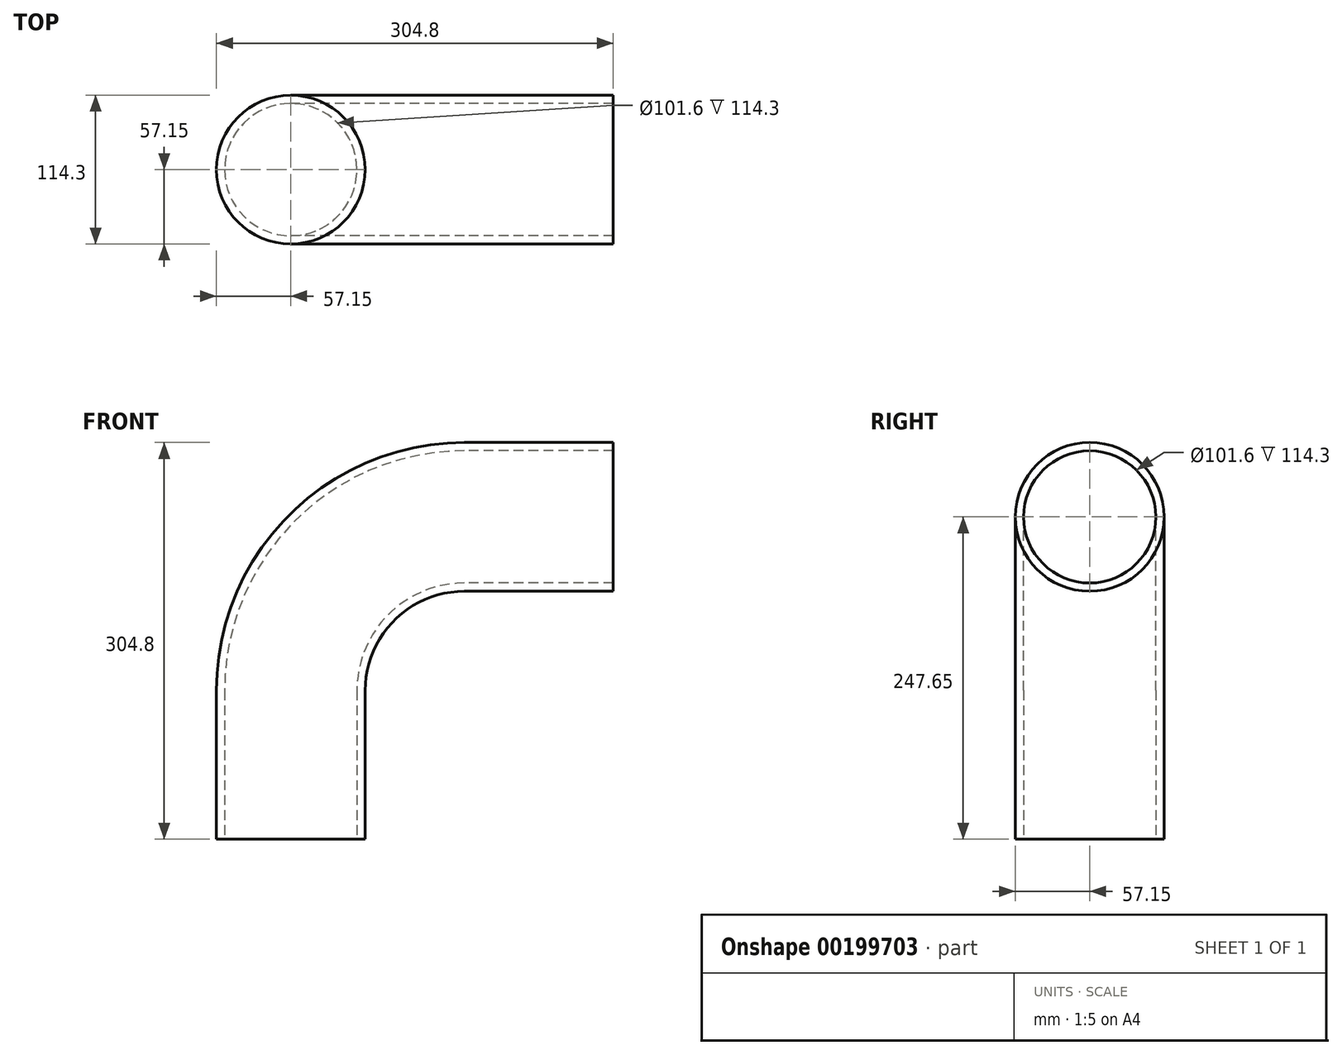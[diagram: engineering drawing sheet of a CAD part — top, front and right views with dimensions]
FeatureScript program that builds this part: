
annotation { "Feature Type Name" : "Feature", "Feature Type Description" : "" }
export const myFeature = defineFeature(function(context is Context, id is Id, definition is map)
    precondition{}
    {
        {
            var Q0;
            Q0=qCreatedBy(makeId("Front.planeOp"),FACE);
            var sketch = newSketch(context, id + "F0", { "sketchPlane" : qUnion([Q0])});
            skLineSegment(sketch, "E0.bottom", {"start": v(0, 0) * mm, "end": v(114.3, 0) * mm});
            skLineSegment(sketch, "E0.top", {"start": v(190.5, 304.8) * mm, "end": v(304.8, 304.8) * mm});
            skLineSegment(sketch, "E0.left", {"start": v(0, 0) * mm, "end": v(0, 114.3) * mm});
            skLineSegment(sketch, "E0.right", {"start": v(304.8, 190.5) * mm, "end": v(304.8, 304.8) * mm});
            skLineSegment(sketch, "E1.right", {"start": v(114.3, 0) * mm, "end": v(114.3, 114.3) * mm});
            skLineSegment(sketch, "E2.top", {"start": v(304.8, 190.5) * mm, "end": v(190.5, 190.5) * mm});
            skArc(sketch, "E3", {"start": v(190.5, 190.5) * mm, "mid": v(136.62, 168.18) * mm, "end": v(114.3, 114.3) * mm});
            skArc(sketch, "E4", {"start": v(190.5, 304.8) * mm, "mid": v(55.8, 249) * mm, "end": v(0, 114.3) * mm});
            skSolve(sketch);
        }
        {
            var Q0;
            Q0=makeQuery(id+"F0.imprint","IMPRINT",FACE,{"disambiguationData":[TD([[makeQuery(id+"F0.imprint","IMPRINT",EDGE,{"derivedFrom":sQuery(id+"F0.wireOp",EDGE,"E0.bottom")}),1.0]])]});
            extrude(context, id + "F1", {"entities" : qUnion([Q0]), "endBound" : BoundingType.SYMMETRIC, "depth" : 114.3 * mm});
        }
        {
            var Q0;
            Q0=makeQuery(id+"F1.opExtrude","CAP_EDGE",EDGE,{"disambiguationData":[OSD([sQuery(id+"F0.wireOp",EDGE,"E1.right")])],"isStart":false});
            var Q1;
            Q1=makeQuery(id+"F1.opExtrude","CAP_EDGE",EDGE,{"disambiguationData":[OSD([sQuery(id+"F0.wireOp",EDGE,"E1.right")])],"isStart":true});
            var Q2;
            Q2=makeQuery(id+"F1.opExtrude","CAP_EDGE",EDGE,{"disambiguationData":[OSD([sQuery(id+"F0.wireOp",EDGE,"E0.top")])],"isStart":false});
            var Q3;
            Q3=makeQuery(id+"F1.opExtrude","CAP_EDGE",EDGE,{"disambiguationData":[OSD([sQuery(id+"F0.wireOp",EDGE,"E0.top")])],"isStart":true});
            fillet(context, id + "F2", {"entities" : qUnion([Q0, Q1, Q2, Q3]), "radius" : 57.15 * mm, "tangentPropagation" : true, "allowEdgeOverflow" : false});
        }
        {
            var Q0;
            Q0=makeQuery(id+"F1.opExtrude","SWEPT_FACE",FACE,{"disambiguationData":[OSD([sQuery(id+"F0.wireOp",EDGE,"E0.right")])]});
            var Q1;
            Q1=makeQuery(id+"F1.opExtrude","SWEPT_FACE",FACE,{"disambiguationData":[OSD([sQuery(id+"F0.wireOp",EDGE,"E0.bottom")])]});
            shell(context, id + "F3", {"entities" : qUnion([Q0, Q1]), "thickness" : 6.35 * mm});
        }
    });
